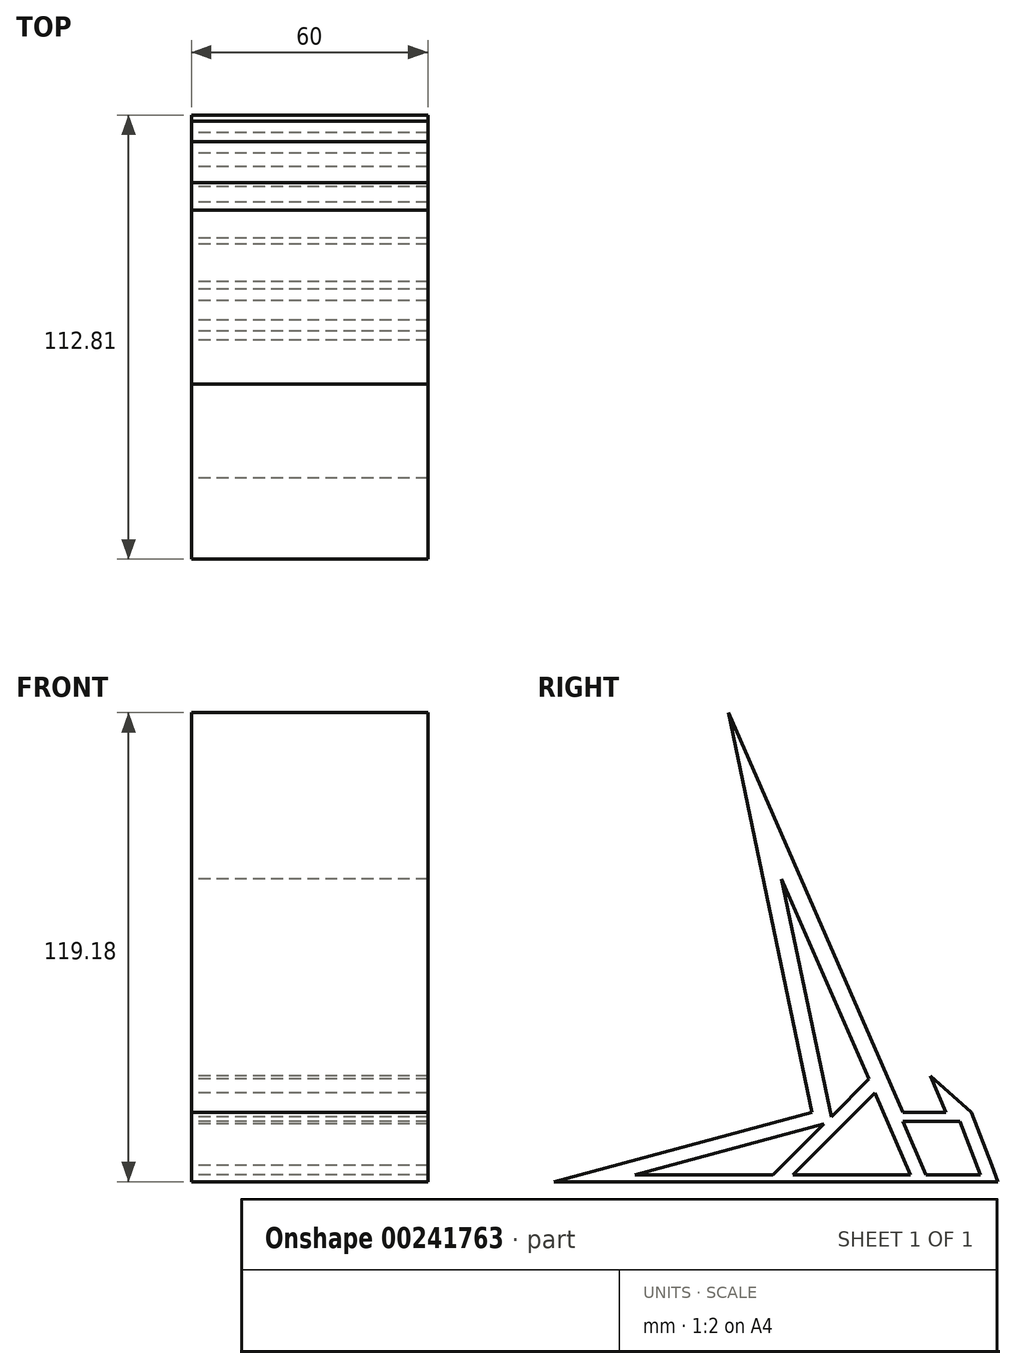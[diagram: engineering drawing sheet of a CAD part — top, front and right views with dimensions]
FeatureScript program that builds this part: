
annotation { "Feature Type Name" : "Feature", "Feature Type Description" : "" }
export const myFeature = defineFeature(function(context is Context, id is Id, definition is map)
    precondition{}
    {
        {
            var Q0;
            Q0=qCreatedBy(makeId("Right.planeOp"),FACE);
            var sketch = newSketch(context, id + "F0", { "sketchPlane" : qUnion([Q0])});
            skLineSegment(sketch, "E0", {"start": v(11.56, -16.66) * mm, "end": v(-9.65, 84.86) * mm});
            skLineSegment(sketch, "E1", {"start": v(-9.65, 84.86) * mm, "end": v(34.61, -16.66) * mm});
            skLineSegment(sketch, "E2", {"start": v(34.61, -16.66) * mm, "end": v(45.61, -16.66) * mm});
            skLineSegment(sketch, "E3", {"start": v(3.8, 42.6) * mm, "end": v(16.43, -17.8) * mm});
            skLineSegment(sketch, "E4", {"start": v(25.99, -8.26) * mm, "end": v(16.43, -17.8) * mm});
            skLineSegment(sketch, "E5.trimOffspring", {"start": v(25.99, -8.26) * mm, "end": v(3.8, 42.6) * mm});
            skLineSegment(sketch, "E6", {"start": v(45.61, -19) * mm, "end": v(34.6, -19) * mm});
            skPoint(sketch, "E7.orphan", {"position": v(40.1, -19) * mm});
            skLineSegment(sketch, "E8", {"start": v(34.6, -19) * mm, "end": v(38.14, -27.1) * mm});
            skLineSegment(sketch, "E9", {"start": v(57.2, -30.14) * mm, "end": v(52.03, -16.66) * mm});
            skPoint(sketch, "E10.end.orphan", {"position": v(38.35, 0) * mm});
            skLineSegment(sketch, "E11", {"start": v(45.61, -16.66) * mm, "end": v(45.62, -16.66) * mm});
            skLineSegment(sketch, "E12", {"start": v(45.62, -16.66) * mm, "end": v(41.62, -7.49) * mm});
            skLineSegment(sketch, "E13", {"start": v(41.62, -7.49) * mm, "end": v(52.03, -16.66) * mm});
            skPoint(sketch, "E14.start.orphan", {"position": v(50.22, -19) * mm});
            skLineSegment(sketch, "E15", {"start": v(45.61, -19) * mm, "end": v(49.07, -19) * mm});
            skLineSegment(sketch, "E16", {"start": v(11.56, -16.66) * mm, "end": v(-54.07, -34.32) * mm});
            skLineSegment(sketch, "E17", {"start": v(-54.07, -34.32) * mm, "end": v(58.74, -34.32) * mm});
            skLineSegment(sketch, "E18", {"start": v(58.74, -34.32) * mm, "end": v(57.2, -30.14) * mm});
            skLineSegment(sketch, "E19", {"start": v(14.55, -19.68) * mm, "end": v(-33.48, -32.6) * mm});
            skLineSegment(sketch, "E20", {"start": v(-33.48, -32.6) * mm, "end": v(1.6, -32.6) * mm});
            skLineSegment(sketch, "E21", {"start": v(1.6, -32.6) * mm, "end": v(14.55, -19.68) * mm});
            skLineSegment(sketch, "E22", {"start": v(27.53, -11.8) * mm, "end": v(6.7, -32.6) * mm});
            skLineSegment(sketch, "E23", {"start": v(27.53, -11.8) * mm, "end": v(36.6, -32.6) * mm});
            skLineSegment(sketch, "E24", {"start": v(6.7, -32.6) * mm, "end": v(36.6, -32.6) * mm});
            skLineSegment(sketch, "E25", {"start": v(34.6, -19) * mm, "end": v(40.53, -32.6) * mm});
            skLineSegment(sketch, "E26", {"start": v(54.28, -32.6) * mm, "end": v(40.53, -32.6) * mm});
            skPoint(sketch, "E27.start.orphan", {"position": v(52.17, -27.1) * mm});
            skLineSegment(sketch, "E28", {"start": v(49.07, -19) * mm, "end": v(54.28, -32.6) * mm});
            skSolve(sketch);
        }
        {
            var Q0;
            Q0=makeQuery(id+"F0.imprint","IMPRINT",FACE,{"disambiguationData":[TD([[makeQuery(id+"F0.imprint","IMPRINT",EDGE,{"derivedFrom":sQuery(id+"F0.wireOp",EDGE,"KnTdib1U-skGr-HGgK-Y9Qu-JsrhuzUVnTur")}),1.0]])]});
            var Q1;
            Q1=makeQuery(id+"F0.imprint","IMPRINT",FACE,{"disambiguationData":[TD([[makeQuery(id+"F0.imprint","IMPRINT",EDGE,{"derivedFrom":sQuery(id+"F0.wireOp",EDGE,"E0")}),-1.0]])]});
            extrude(context, id + "F1", {"entities" : qUnion([Q0, Q1]), "depth" : 60 * mm});
        }
    });
